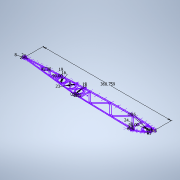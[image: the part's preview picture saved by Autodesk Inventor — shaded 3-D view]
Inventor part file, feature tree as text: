
AUTODESK INVENTOR PART (.ipt)
format: ipt  version: 2022 (Build 260153000, 153)  size: 268,288 bytes
history: native  units: mm
features: sketch x1
ambient origin geometry x8: Origin, YZ Plane, XZ Plane, XY Plane, X Axis, Y Axis, Z Axis, Center Point
feature tree (1):
  sketch  "Sketch1"  dims[d31=34.456mm d50=368.759386mm d57=16.0mm d69=8.0mm d70=23.0mm d71=8.0mm d73=16.0mm d80=19.0mm d81=16.0mm d82=1.0mm d83=1.0mm d84=1.0mm d85=1.0mm d86=1.0mm d87=0.8mm d88=1.0mm d90=19.0mm d94=5.0mm d95=5.0mm d105=5.0mm d106=5.0mm d108=2.0mm d109=19.0mm d114=5.0mm d115=5.0mm d116=24.0mm d117=2.5mm d118=2.5mm d123=2.5mm d124=2.5mm d125=10.0mm d126=24.0mm d127=24.0mm d128=27.0mm d135=0.5mm d136=45.0deg d139=7.0mm d165=45.0deg d169=27.0mm d175=90.0deg d181=45.0deg d185=7.0mm d186=45.0deg d190=7.0mm d191=45.0deg d197=90.0deg d203=90.0deg d206=7.0mm]
